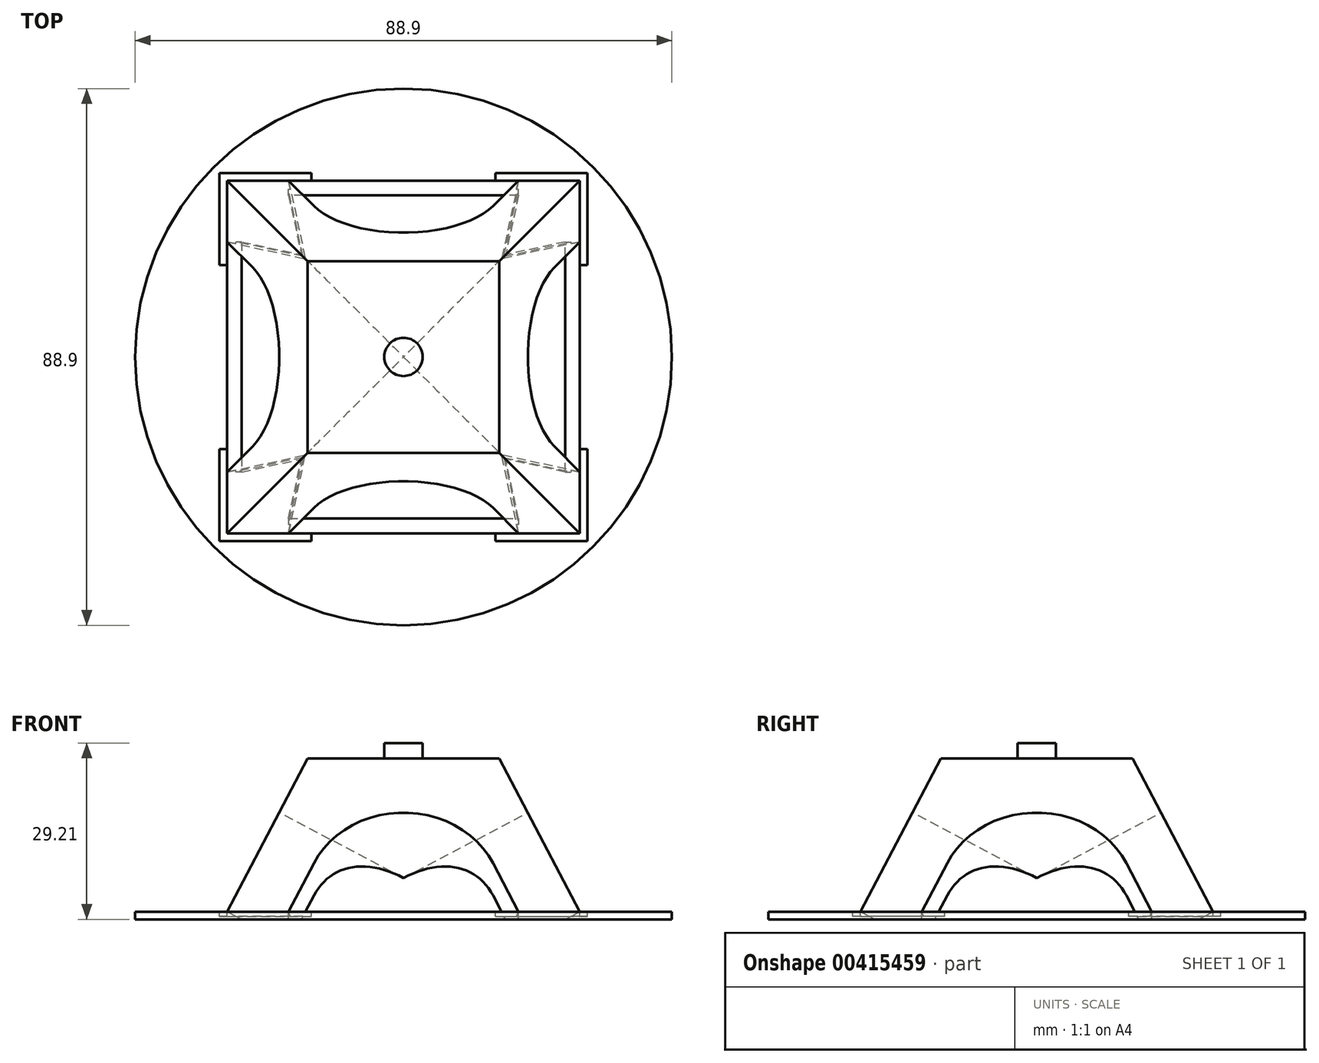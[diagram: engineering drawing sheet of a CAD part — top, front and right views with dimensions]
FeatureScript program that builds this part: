
annotation { "Feature Type Name" : "Feature", "Feature Type Description" : "" }
export const myFeature = defineFeature(function(context is Context, id is Id, definition is map)
    precondition{}
    {
        {
            var Q0;
            Q0=qCreatedBy(makeId("Top.planeOp"),FACE);
            var sketch = newSketch(context, id + "F0", { "sketchPlane" : qUnion([Q0])});
            skCircle(sketch, "E0", {"center": v(0, 0) * mm, "radius": 44.45 * mm});
            skCircle(sketch, "E1", {"center": v(0, 0) * mm, "radius": 3.81 * mm});
            skSolve(sketch);
        }
        {
            var Q0;
            Q0=makeQuery(id+"F0.imprint","IMPRINT",FACE,{"disambiguationData":[TD([[makeQuery(id+"F0.imprint","IMPRINT",EDGE,{"derivedFrom":sQuery(id+"F0.wireOp",EDGE,"E0")}),1.0]])]});
            extrude(context, id + "F1", {"entities" : qUnion([Q0]), "oppositeDirection" : true, "depth" : 1.27 * mm});
        }
        {
            var Q0;
            Q0=qCreatedBy(makeId("Top.planeOp"),FACE);
            var sketch = newSketch(context, id + "F2", { "sketchPlane" : qUnion([Q0])});
            skLineSegment(sketch, "E2.bottom", {"start": v(-29.2, 29.21) * mm, "end": v(29.21, 29.21) * mm});
            skLineSegment(sketch, "E2.top", {"start": v(-29.21, -29.2) * mm, "end": v(29.2, -29.2) * mm});
            skLineSegment(sketch, "E2.left", {"start": v(-29.2, 29.21) * mm, "end": v(-29.21, -29.2) * mm});
            skLineSegment(sketch, "E2.right", {"start": v(29.21, 29.21) * mm, "end": v(29.2, -29.2) * mm});
            skPoint(sketch, "E2.middle", {"position": v(0, 0) * mm});
            skSolve(sketch);
        }
        {
            var Q0;
            Q0=qCreatedBy(makeId("Top.planeOp"),FACE);
            cPlane(context, id + "F3", {"entities" : qUnion([Q0]), "cplaneType" : CPlaneType.OFFSET, "offset" : 25.4 * mm, "width" : 152.4 * mm, "height" : 152.4 * mm});
        }
        {
            var Q0;
            Q0=qCreatedBy(id+"F3.planeOp",FACE);
            var sketch = newSketch(context, id + "F4", { "sketchPlane" : qUnion([Q0])});
            skLineSegment(sketch, "E3.bottom", {"start": v(-15.88, 15.88) * mm, "end": v(15.88, 15.88) * mm});
            skLineSegment(sketch, "E3.top", {"start": v(-15.88, -15.88) * mm, "end": v(15.88, -15.88) * mm});
            skLineSegment(sketch, "E3.left", {"start": v(-15.88, 15.88) * mm, "end": v(-15.88, -15.88) * mm});
            skLineSegment(sketch, "E3.right", {"start": v(15.88, 15.88) * mm, "end": v(15.88, -15.87) * mm});
            skPoint(sketch, "E3.middle", {"position": v(0, 0) * mm});
            skSolve(sketch);
        }
        {
            var Q1;
            Q1=makeQuery(id+"F2.imprint","IMPRINT",FACE,{"disambiguationData":[TD([[makeQuery(id+"F2.imprint","IMPRINT",EDGE,{"derivedFrom":sQuery(id+"F2.wireOp",EDGE,"E2.bottom")}),-1.0]])]});
            var Q2;
            Q2=makeQuery(id+"F4.imprint","IMPRINT",FACE,{"disambiguationData":[TD([[makeQuery(id+"F4.imprint","IMPRINT",EDGE,{"derivedFrom":sQuery(id+"F4.wireOp",EDGE,"E3.bottom")}),-1.0]])]});
            loft(context, id + "F5", {"sheetProfilesArray" : [{ "sheetProfileEntities" : qUnion([Q1]) }, { "sheetProfileEntities" : qUnion([Q2]) }]});
        }
        {
            var Q0;
            Q0=makeQuery(id+"F5.opLoft","SWEPT_FACE",FACE,{"disambiguationData":[OSD([sQuery(id+"F2.wireOp",EDGE,"E2.top"),sQuery(id+"F2.wireOp",EDGE,"E2.left"),sQuery(id+"F2.wireOp",EDGE,"E2.right"),sQuery(id+"F4.wireOp",EDGE,"E3.top"),sQuery(id+"F4.wireOp",EDGE,"E3.left"),sQuery(id+"F4.wireOp",EDGE,"E3.right")])]});
            var sketch = newSketch(context, id + "F6", { "sketchPlane" : qUnion([Q0])});
            skLineSegment(sketch, "E4.0.0", {"start": v(29.2, -13.58) * mm, "end": v(15.87, 15.1) * mm});
            skLineSegment(sketch, "E4.0.1", {"start": v(15.88, 15.1) * mm, "end": v(-15.88, 15.1) * mm});
            skLineSegment(sketch, "E4.0.2", {"start": v(-15.87, 15.1) * mm, "end": v(-29.21, -13.58) * mm});
            skLineSegment(sketch, "E4.0.3", {"start": v(-29.21, -13.58) * mm, "end": v(29.2, -13.58) * mm});
            skLineSegment(sketch, "E5", {"start": v(-19.05, -13.58) * mm, "end": v(-14.84, -4.52) * mm});
            skLineSegment(sketch, "E6", {"start": v(19.05, -13.58) * mm, "end": v(14.84, -4.52) * mm});
            skArc(sketch, "E7", {"start": v(14.84, -4.52) * mm, "mid": v(0, 4.95) * mm, "end": v(-14.84, -4.52) * mm});
            skSolve(sketch);
        }
        {
            var Q0;
            Q0=makeQuery(id+"F5.opLoft","SWEPT_FACE",FACE,{"disambiguationData":[OSD([sQuery(id+"F2.wireOp",EDGE,"E2.bottom"),sQuery(id+"F2.wireOp",EDGE,"E2.top"),sQuery(id+"F2.wireOp",EDGE,"E2.right"),sQuery(id+"F4.wireOp",EDGE,"E3.bottom"),sQuery(id+"F4.wireOp",EDGE,"E3.top"),sQuery(id+"F4.wireOp",EDGE,"E3.right")])]});
            var sketch = newSketch(context, id + "F7", { "sketchPlane" : qUnion([Q0])});
            skLineSegment(sketch, "E8.0.0", {"start": v(29.21, -13.58) * mm, "end": v(15.87, 15.1) * mm});
            skLineSegment(sketch, "E8.0.1", {"start": v(-15.87, 15.1) * mm, "end": v(15.88, 15.1) * mm});
            skLineSegment(sketch, "E8.0.2", {"start": v(-15.87, 15.1) * mm, "end": v(-29.2, -13.58) * mm});
            skLineSegment(sketch, "E8.0.3", {"start": v(-29.2, -13.58) * mm, "end": v(29.21, -13.58) * mm});
            skLineSegment(sketch, "E9", {"start": v(-19.05, -13.58) * mm, "end": v(-14.84, -4.52) * mm});
            skLineSegment(sketch, "E10", {"start": v(19.05, -13.58) * mm, "end": v(14.84, -4.52) * mm});
            skArc(sketch, "E11", {"start": v(14.84, -4.52) * mm, "mid": v(0, 4.95) * mm, "end": v(-14.84, -4.52) * mm});
            skSolve(sketch);
        }
        {
            var Q0;
            Q0=makeQuery(id+"F5.opLoft","SWEPT_FACE",FACE,{"disambiguationData":[OSD([sQuery(id+"F2.wireOp",EDGE,"E2.bottom"),sQuery(id+"F2.wireOp",EDGE,"E2.left"),sQuery(id+"F2.wireOp",EDGE,"E2.right"),sQuery(id+"F4.wireOp",EDGE,"E3.bottom"),sQuery(id+"F4.wireOp",EDGE,"E3.left"),sQuery(id+"F4.wireOp",EDGE,"E3.right")])]});
            var sketch = newSketch(context, id + "F8", { "sketchPlane" : qUnion([Q0])});
            skLineSegment(sketch, "E12.0.0", {"start": v(-15.88, 15.1) * mm, "end": v(15.88, 15.1) * mm});
            skLineSegment(sketch, "E12.0.1", {"start": v(-15.88, 15.1) * mm, "end": v(-29.21, -13.58) * mm});
            skLineSegment(sketch, "E12.0.2", {"start": v(-29.21, -13.58) * mm, "end": v(29.2, -13.58) * mm});
            skLineSegment(sketch, "E12.0.3", {"start": v(29.2, -13.58) * mm, "end": v(15.88, 15.1) * mm});
            skLineSegment(sketch, "E13", {"start": v(-19.05, -13.58) * mm, "end": v(-14.84, -4.52) * mm});
            skLineSegment(sketch, "E14", {"start": v(19.05, -13.58) * mm, "end": v(14.84, -4.52) * mm});
            skArc(sketch, "E15", {"start": v(14.84, -4.52) * mm, "mid": v(0, 4.95) * mm, "end": v(-14.84, -4.52) * mm});
            skSolve(sketch);
        }
        {
            var Q0;
            Q0=makeQuery(id+"F5.opLoft","SWEPT_FACE",FACE,{"disambiguationData":[OSD([sQuery(id+"F2.wireOp",EDGE,"E2.bottom"),sQuery(id+"F2.wireOp",EDGE,"E2.top"),sQuery(id+"F2.wireOp",EDGE,"E2.left"),sQuery(id+"F4.wireOp",EDGE,"E3.bottom"),sQuery(id+"F4.wireOp",EDGE,"E3.top"),sQuery(id+"F4.wireOp",EDGE,"E3.left")])]});
            var sketch = newSketch(context, id + "F9", { "sketchPlane" : qUnion([Q0])});
            skLineSegment(sketch, "E16.0.0", {"start": v(29.2, -13.58) * mm, "end": v(15.88, 15.1) * mm});
            skLineSegment(sketch, "E16.0.1", {"start": v(15.88, 15.1) * mm, "end": v(-15.87, 15.1) * mm});
            skLineSegment(sketch, "E16.0.2", {"start": v(-15.88, 15.1) * mm, "end": v(-29.21, -13.58) * mm});
            skLineSegment(sketch, "E16.0.3", {"start": v(-29.21, -13.58) * mm, "end": v(29.2, -13.58) * mm});
            skLineSegment(sketch, "E17", {"start": v(-19.05, -13.58) * mm, "end": v(-14.84, -4.52) * mm});
            skLineSegment(sketch, "E18", {"start": v(19.05, -13.58) * mm, "end": v(14.84, -4.52) * mm});
            skArc(sketch, "E19", {"start": v(14.84, -4.52) * mm, "mid": v(0, 4.95) * mm, "end": v(-14.84, -4.52) * mm});
            skSolve(sketch);
        }
        {
            var Q0;
            {var subQ0=sQuery(id+"F7.wireOp",EDGE,"E9");Q0=makeQuery(id+"F7.imprint","IMPRINT",FACE,{"disambiguationData":[TD([[makeQuery(id+"F7.imprint","IMPRINT",EDGE,{"derivedFrom":subQ0}),-1.0]])]});}
            extrude(context, id + "F10", {"entities" : qUnion([Q0]), "operationType" : NewBodyOperationType.REMOVE, "oppositeDirection" : true, "depth" : 141.48 * mm});
        }
        {
            var Q0;
            {var subQ0=sQuery(id+"F8.wireOp",EDGE,"E13");Q0=makeQuery(id+"F8.imprint","IMPRINT",FACE,{"disambiguationData":[TD([[makeQuery(id+"F8.imprint","IMPRINT",EDGE,{"derivedFrom":subQ0}),-1.0]])]});}
            extrude(context, id + "F11", {"entities" : qUnion([Q0]), "operationType" : NewBodyOperationType.REMOVE, "oppositeDirection" : true, "depth" : 70.87 * mm});
        }
        {
            var Q0;
            {var subQ0=sQuery(id+"F9.wireOp",EDGE,"E17");Q0=makeQuery(id+"F9.imprint","IMPRINT",FACE,{"disambiguationData":[TD([[makeQuery(id+"F9.imprint","IMPRINT",EDGE,{"derivedFrom":subQ0}),-1.0]])]});}
            extrude(context, id + "F12", {"entities" : qUnion([Q0]), "operationType" : NewBodyOperationType.REMOVE, "oppositeDirection" : true, "depth" : 64.52 * mm});
        }
        {
            var Q0;
            {var subQ0=sQuery(id+"F6.wireOp",EDGE,"E5");Q0=makeQuery(id+"F6.imprint","IMPRINT",FACE,{"disambiguationData":[TD([[makeQuery(id+"F6.imprint","IMPRINT",EDGE,{"derivedFrom":subQ0}),-1.0]])]});}
            extrude(context, id + "F13", {"entities" : qUnion([Q0]), "operationType" : NewBodyOperationType.REMOVE, "oppositeDirection" : true, "depth" : 65.28 * mm});
        }
        {
            var Q0;
            Q0=makeQuery(id+"F1.opExtrude","CAP_FACE",FACE,{"disambiguationData":[OSD([sQuery(id+"F0.wireOp",EDGE,"E0")])],"isStart":true});
            var sketch = newSketch(context, id + "F14", { "sketchPlane" : qUnion([Q0])});
            skCircle(sketch, "E20.0.0", {"center": v(0, 0) * mm, "radius": 44.45 * mm});
            skLineSegment(sketch, "E21", {"start": v(0, 0) * mm, "end": v(0, 44.45) * mm, "construction": true});
            skLineSegment(sketch, "E22", {"start": v(0, 0) * mm, "end": v(0, -44.45) * mm, "construction": true});
            skLineSegment(sketch, "E23", {"start": v(0, 0) * mm, "end": v(44.45, 0) * mm, "construction": true});
            skLineSegment(sketch, "E24", {"start": v(0, 0) * mm, "end": v(-44.45, 0) * mm, "construction": true});
            skLineSegment(sketch, "E25.bottom", {"start": v(-30.48, 30.48) * mm, "end": v(30.48, 30.48) * mm});
            skLineSegment(sketch, "E25.top", {"start": v(-30.48, -30.48) * mm, "end": v(30.48, -30.48) * mm});
            skLineSegment(sketch, "E25.left", {"start": v(-30.48, 30.48) * mm, "end": v(-30.48, -30.48) * mm});
            skLineSegment(sketch, "E25.right", {"start": v(30.48, 30.48) * mm, "end": v(30.48, -30.48) * mm});
            skLineSegment(sketch, "E26", {"start": v(-15.24, 41.76) * mm, "end": v(-15.24, -41.76) * mm});
            skLineSegment(sketch, "E27", {"start": v(15.24, -41.76) * mm, "end": v(15.24, 41.76) * mm});
            skLineSegment(sketch, "E28", {"start": v(-41.76, 15.24) * mm, "end": v(41.76, 15.24) * mm});
            skLineSegment(sketch, "E29", {"start": v(41.76, -15.24) * mm, "end": v(-41.76, -15.24) * mm});
            skSolve(sketch);
        }
        {
            var Q0;
            {var subQ0=sQuery(id+"F14.wireOp",EDGE,"E25.left");var subQ1=sQuery(id+"F14.wireOp",EDGE,"E25.bottom");var subQ2=makeQuery(id+"F14.imprint","INTERSECT",VERTEX,{"derivedFrom":[subQ1,subQ0]});Q0=makeQuery(id+"F14.imprint","IMPRINT",FACE,{"disambiguationData":[TD([[makeQuery(id+"F14.imprint","IMPRINT",EDGE,{"disambiguationData":[TD([[subQ2,-1.0]])],"derivedFrom":subQ1}),-1.0]])]});}
            var Q1;
            {var subQ0=sQuery(id+"F14.wireOp",EDGE,"E25.right");var subQ1=sQuery(id+"F14.wireOp",EDGE,"E25.bottom");var subQ2=makeQuery(id+"F14.imprint","INTERSECT",VERTEX,{"derivedFrom":[subQ1,subQ0]});Q1=makeQuery(id+"F14.imprint","IMPRINT",FACE,{"disambiguationData":[TD([[makeQuery(id+"F14.imprint","IMPRINT",EDGE,{"disambiguationData":[TD([[subQ2,1.0]])],"derivedFrom":subQ1}),-1.0]])]});}
            var Q2;
            {var subQ0=sQuery(id+"F14.wireOp",EDGE,"E25.right");var subQ1=sQuery(id+"F14.wireOp",EDGE,"E25.top");var subQ2=makeQuery(id+"F14.imprint","INTERSECT",VERTEX,{"derivedFrom":[subQ1,subQ0]});Q2=makeQuery(id+"F14.imprint","IMPRINT",FACE,{"disambiguationData":[TD([[makeQuery(id+"F14.imprint","IMPRINT",EDGE,{"disambiguationData":[TD([[subQ2,1.0]])],"derivedFrom":subQ1}),1.0]])]});}
            var Q3;
            {var subQ0=sQuery(id+"F14.wireOp",EDGE,"E25.left");var subQ1=sQuery(id+"F14.wireOp",EDGE,"E25.top");var subQ2=makeQuery(id+"F14.imprint","INTERSECT",VERTEX,{"derivedFrom":[subQ1,subQ0]});Q3=makeQuery(id+"F14.imprint","IMPRINT",FACE,{"disambiguationData":[TD([[makeQuery(id+"F14.imprint","IMPRINT",EDGE,{"disambiguationData":[TD([[subQ2,-1.0]])],"derivedFrom":subQ1}),1.0]])]});}
            extrude(context, id + "F15", {"entities" : qUnion([Q0, Q1, Q2, Q3]), "operationType" : NewBodyOperationType.REMOVE, "oppositeDirection" : true, "depth" : 0.76 * mm});
        }
        {
            var Q0;
            Q0=makeQuery(id+"F5.opLoft","CAP_FACE",FACE,{"disambiguationData":[OSD([makeQuery(id+"F4.imprint","IMPRINT",FACE,{"disambiguationData":[TD([[makeQuery(id+"F4.imprint","IMPRINT",EDGE,{"derivedFrom":sQuery(id+"F4.wireOp",EDGE,"E3.bottom")}),-1.0]])]})])],"isStart":true});
            var sketch = newSketch(context, id + "F16", { "sketchPlane" : qUnion([Q0])});
            skCircle(sketch, "E30", {"center": v(0, 0) * mm, "radius": 3.18 * mm});
            skSolve(sketch);
        }
        {
            var Q0;
            Q0=makeQuery(id+"F16.imprint","IMPRINT",FACE,{"disambiguationData":[TD([[makeQuery(id+"F16.imprint","IMPRINT",EDGE,{"derivedFrom":sQuery(id+"F16.wireOp",EDGE,"E30")}),1.0]])]});
            extrude(context, id + "F17", {"entities" : qUnion([Q0]), "operationType" : NewBodyOperationType.ADD, "depth" : 2.54 * mm});
        }
    });
